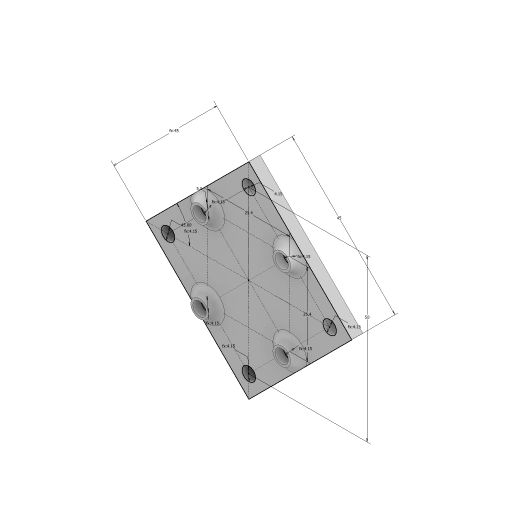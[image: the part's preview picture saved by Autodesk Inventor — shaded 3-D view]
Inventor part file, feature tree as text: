
AUTODESK INVENTOR PART (.ipt)
format: ipt  version: 2023 (Build 270158000, 158)  size: 174,592 bytes
history: native  units: mm
features: sketch x2, extrude x2, fillet x1
ambient origin geometry x8: Origin, YZ Plane, XZ Plane, XY Plane, X Axis, Y Axis, Z Axis, Center Point
bodies: Solid1 (feature_tree)
feature tree (5):
  sketch  "Sketch1"  dims[d0=50.0mm d1=4.15mm]
  extrude  "Extrusion1"  Depth=4.15mm
  extrude  "Extrusion2"  Depth=2.5mm
  sketch  "Sketch Driven Pattern1"  dims[d2=4.15mm d3=4.15mm d4=4.15mm d5=25.4mm d6=25.4mm d7=4.15mm d8=4.15mm d9=4.15mm d10=4.15mm d11=5.5mm d12=45.0deg d13=45.0mm d18=45.0mm d22=3.5mm d23=0.0mm d24=2.5mm d25=0.0mm d26=2.5mm]
  fillet  "Fillet1"  Radius=4.15mm
